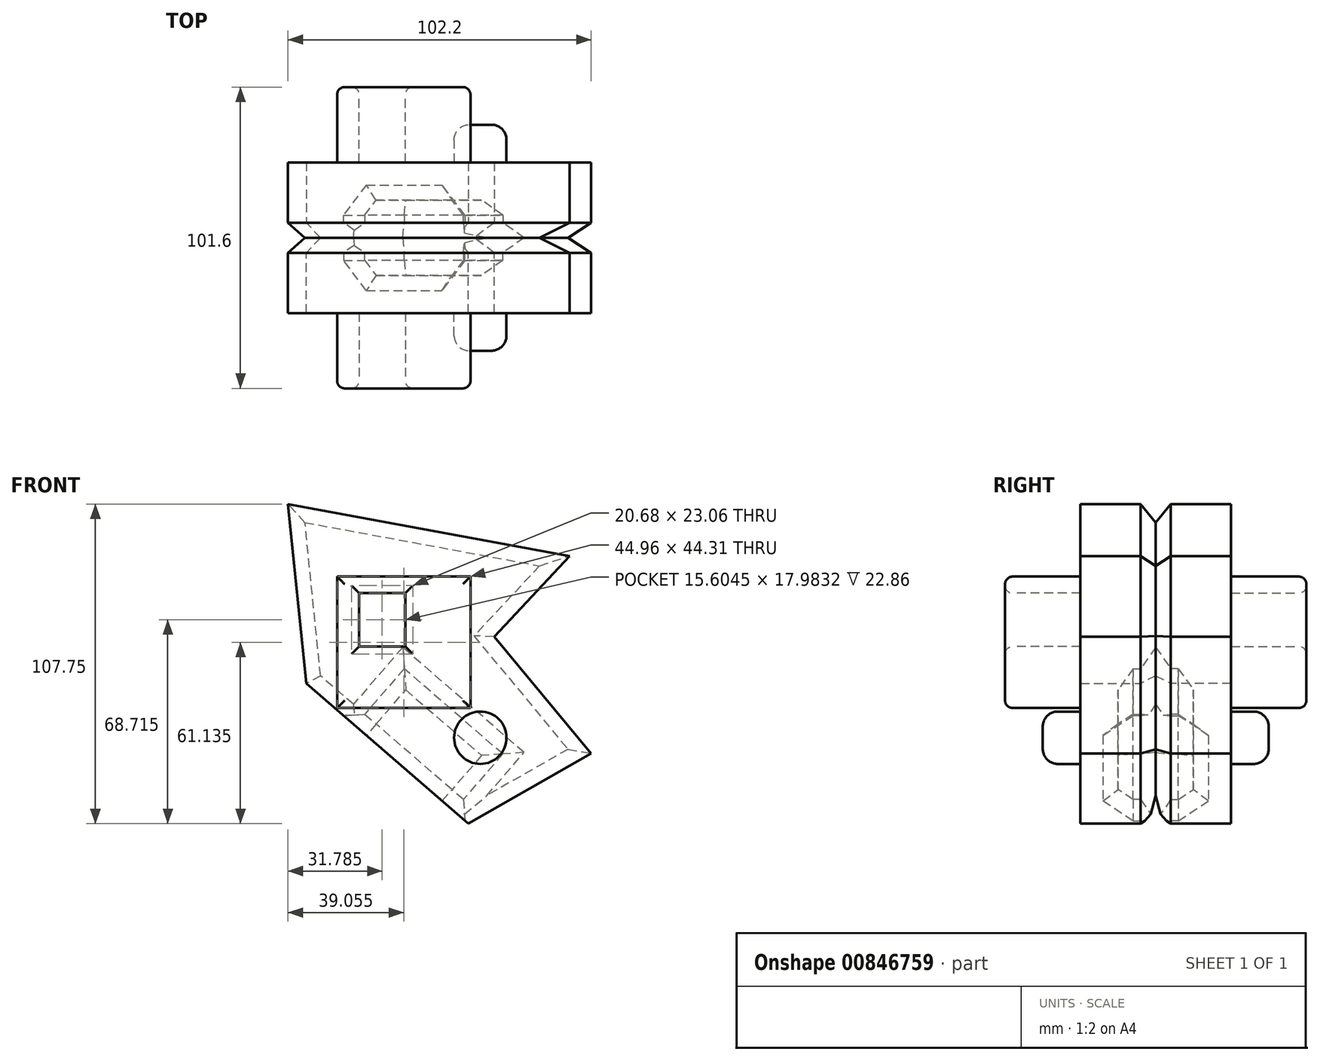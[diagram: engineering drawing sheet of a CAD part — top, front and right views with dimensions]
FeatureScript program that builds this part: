
annotation { "Feature Type Name" : "Feature", "Feature Type Description" : "" }
export const myFeature = defineFeature(function(context is Context, id is Id, definition is map)
    precondition{}
    {
        {
            var Q0;
            Q0=qCreatedBy(makeId("Front.planeOp"),FACE);
            var sketch = newSketch(context, id + "F0", { "sketchPlane" : qUnion([Q0])});
            skLineSegment(sketch, "E0", {"start": v(-47.16, 68.77) * mm, "end": v(47.74, 51.25) * mm});
            skLineSegment(sketch, "E1", {"start": v(47.74, 51.25) * mm, "end": v(22.34, 24.1) * mm});
            skLineSegment(sketch, "E2", {"start": v(22.34, 24.1) * mm, "end": v(55.04, -15.33) * mm});
            skLineSegment(sketch, "E3", {"start": v(55.04, -15.33) * mm, "end": v(13.58, -38.98) * mm});
            skLineSegment(sketch, "E4", {"start": v(13.58, -38.98) * mm, "end": v(-41.03, 8.32) * mm});
            skLineSegment(sketch, "E5", {"start": v(-41.03, 8.32) * mm, "end": v(-47.16, 68.77) * mm});
            skSolve(sketch);
        }
        {
            var Q0;
            Q0=makeQuery(id+"F0.imprint","IMPRINT",FACE,{"disambiguationData":[TD([[makeQuery(id+"F0.imprint","IMPRINT",EDGE,{"derivedFrom":sQuery(id+"F0.wireOp",EDGE,"E0")}),-1.0]])]});
            extrude(context, id + "F1", {"entities" : qUnion([Q0]), "depth" : 25.4 * mm, "offsetDistance" : 25.4 * mm});
        }
        {
            var Q0;
            Q0=makeQuery(id+"F1.opExtrude","CAP_FACE",FACE,{"disambiguationData":[OSD([sQuery(id+"F0.wireOp",EDGE,"E0"),sQuery(id+"F0.wireOp",EDGE,"E1"),sQuery(id+"F0.wireOp",EDGE,"E2"),sQuery(id+"F0.wireOp",EDGE,"E3"),sQuery(id+"F0.wireOp",EDGE,"E4"),sQuery(id+"F0.wireOp",EDGE,"E5")])],"isStart":false});
            var sketch = newSketch(context, id + "F2", { "sketchPlane" : qUnion([Q0])});
            skLineSegment(sketch, "E6.bottom", {"start": v(-30.59, 44.3) * mm, "end": v(14.38, 44.3) * mm});
            skLineSegment(sketch, "E6.top", {"start": v(-30.59, 0) * mm, "end": v(14.38, 0) * mm});
            skLineSegment(sketch, "E6.left", {"start": v(-30.59, 44.3) * mm, "end": v(-30.59, 0) * mm});
            skLineSegment(sketch, "E6.right", {"start": v(14.38, 44.3) * mm, "end": v(14.38, 0) * mm});
            skSolve(sketch);
        }
        {
            var Q0;
            Q0=makeQuery(id+"F2.imprint","IMPRINT",FACE,{"disambiguationData":[TD([[makeQuery(id+"F2.imprint","IMPRINT",EDGE,{"derivedFrom":sQuery(id+"F2.wireOp",EDGE,"E6.bottom")}),-1.0]])]});
            extrude(context, id + "F3", {"entities" : qUnion([Q0]), "operationType" : NewBodyOperationType.ADD, "depth" : 25.4 * mm, "offsetDistance" : 25.4 * mm});
        }
        {
            var Q0;
            Q0=makeQuery(id+"F3.opExtrude","CAP_FACE",FACE,{"disambiguationData":[OSD([sQuery(id+"F2.wireOp",EDGE,"E6.bottom"),sQuery(id+"F2.wireOp",EDGE,"E6.top"),sQuery(id+"F2.wireOp",EDGE,"E6.left"),sQuery(id+"F2.wireOp",EDGE,"E6.right")])],"isStart":false});
            var sketch = newSketch(context, id + "F4", { "sketchPlane" : qUnion([Q0])});
            skLineSegment(sketch, "E7.bottom", {"start": v(-7.57, 20.74) * mm, "end": v(-23.18, 20.74) * mm});
            skLineSegment(sketch, "E7.top", {"start": v(-7.57, 38.73) * mm, "end": v(-23.18, 38.73) * mm});
            skLineSegment(sketch, "E7.left", {"start": v(-7.57, 20.74) * mm, "end": v(-7.57, 38.73) * mm});
            skLineSegment(sketch, "E7.right", {"start": v(-23.18, 20.74) * mm, "end": v(-23.18, 38.73) * mm});
            skPoint(sketch, "E7.middle", {"position": v(-15.37, 29.73) * mm});
            skSolve(sketch);
        }
        {
            var Q0;
            Q0 = qSketchRegion(id + "F4", true);
            extrude(context, id + "F5", {"entities" : qUnion([Q0]), "operationType" : NewBodyOperationType.REMOVE, "oppositeDirection" : true, "depth" : 25.4 * mm, "offsetDistance" : 25.4 * mm});
        }
        {
            var Q0;
            Q0=makeQuery(id+"F1.opExtrude","SWEPT_FACE",FACE,{"disambiguationData":[OSD([sQuery(id+"F0.wireOp",EDGE,"E4")])]});
            var sketch = newSketch(context, id + "F6", { "sketchPlane" : qUnion([Q0])});
            skPoint(sketch, "E8.firstSnap0", {"position": v(-36.46, 12.7) * mm});
            skLineSegment(sketch, "E8.bottom", {"start": v(-14.7, 12.7) * mm, "end": v(29.26, 12.7) * mm});
            skLineSegment(sketch, "E8.top", {"start": v(-14.7, 0) * mm, "end": v(29.26, 0) * mm});
            skLineSegment(sketch, "E8.left", {"start": v(-14.7, 12.7) * mm, "end": v(-14.7, 0) * mm});
            skLineSegment(sketch, "E8.right", {"start": v(29.26, 12.7) * mm, "end": v(29.26, 0) * mm});
            skSolve(sketch);
        }
        {
            var Q0;
            Q0 = qSketchRegion(id + "F6", true);
            extrude(context, id + "F7", {"entities" : qUnion([Q0]), "operationType" : NewBodyOperationType.REMOVE, "oppositeDirection" : true, "depth" : 25.4 * mm, "offsetDistance" : 25.4 * mm});
        }
        {
            var Q0;
            Q0=makeQuery(id+"F1.opExtrude","CAP_FACE",FACE,{"disambiguationData":[OSD([sQuery(id+"F0.wireOp",EDGE,"E0"),sQuery(id+"F0.wireOp",EDGE,"E1"),sQuery(id+"F0.wireOp",EDGE,"E2"),sQuery(id+"F0.wireOp",EDGE,"E3"),sQuery(id+"F0.wireOp",EDGE,"E4"),sQuery(id+"F0.wireOp",EDGE,"E5")])],"isStart":false});
            var sketch = newSketch(context, id + "F8", { "sketchPlane" : qUnion([Q0])});
            skLineSegment(sketch, "E9.bottom", {"start": v(46.14, -13.59) * mm, "end": v(-19.09, -13.59) * mm});
            skLineSegment(sketch, "E9.top", {"start": v(46.14, 0) * mm, "end": v(-19.09, 0) * mm});
            skLineSegment(sketch, "E9.left", {"start": v(46.14, -13.59) * mm, "end": v(46.14, 0) * mm});
            skLineSegment(sketch, "E9.right", {"start": v(-19.09, -13.59) * mm, "end": v(-19.09, 0) * mm});
            skSolve(sketch);
        }
        {
            var Q0;
            Q0=makeQuery(id+"F3.opExtrude","CAP_FACE",FACE,{"disambiguationData":[OSD([sQuery(id+"F2.wireOp",EDGE,"E6.bottom"),sQuery(id+"F2.wireOp",EDGE,"E6.top"),sQuery(id+"F2.wireOp",EDGE,"E6.left"),sQuery(id+"F2.wireOp",EDGE,"E6.right")])],"isStart":false});
            fillet(context, id + "F9", {"entities" : qUnion([Q0]), "radius" : 2.54 * mm, "tangentPropagation" : true, "allowEdgeOverflow" : false});
        }
        {
            var Q0;
            Q0=makeQuery(id+"F1.opExtrude","CAP_FACE",FACE,{"disambiguationData":[OSD([sQuery(id+"F0.wireOp",EDGE,"E0"),sQuery(id+"F0.wireOp",EDGE,"E1"),sQuery(id+"F0.wireOp",EDGE,"E2"),sQuery(id+"F0.wireOp",EDGE,"E3"),sQuery(id+"F0.wireOp",EDGE,"E4"),sQuery(id+"F0.wireOp",EDGE,"E5")])],"isStart":true});
            chamfer(context, id + "F10", {"entities" : qUnion([Q0]), "width" : 5.08 * mm, "tangentPropagation" : true});
        }
        {
            var Q0;
            Q0=makeQuery(id+"F7.boolean.opBoolean","COPY",FACE,{"derivedFrom":makeQuery(id+"F7.opExtrude","SWEPT_FACE",FACE,{"disambiguationData":[OSD([sQuery(id+"F6.wireOp",EDGE,"E8.bottom")])]})});
            chamfer(context, id + "F11", {"entities" : qUnion([Q0]), "width" : 5.08 * mm, "tangentPropagation" : true});
        }
        {
            var Q0;
            {var subQ0=makeQuery(id+"F1.opExtrude","CAP_EDGE",EDGE,{"disambiguationData":[OSD([sQuery(id+"F0.wireOp",EDGE,"E3")])],"isStart":false});Q0=makeQuery(id+"F8.imprint","IMPRINT",FACE,{"disambiguationData":[TD([[makeQuery(id+"F8.imprint","IMPRINT",EDGE,{"derivedFrom":subQ0}),-1.0]])]});}
            var sketch = newSketch(context, id + "F12", { "sketchPlane" : qUnion([Q0])});
            skCircle(sketch, "E10", {"center": v(17.69, -10.03) * mm, "radius": 8.83 * mm});
            skSolve(sketch);
        }
        {
            var Q0;
            Q0 = qSketchRegion(id + "F12", true);
            extrude(context, id + "F13", {"entities" : qUnion([Q0]), "operationType" : NewBodyOperationType.ADD, "depth" : 12.7 * mm, "offsetDistance" : 25.4 * mm});
        }
        {
            var Q0;
            Q0=makeQuery(id+"F13.opExtrude","CAP_EDGE",EDGE,{"disambiguationData":[OSD([sQuery(id+"F12.wireOp",EDGE,"E10")])],"isStart":false});
            fillet(context, id + "F14", {"entities" : qUnion([Q0]), "radius" : 5.08 * mm, "tangentPropagation" : true, "allowEdgeOverflow" : false});
        }
        {
            var Q0;
            Q0=makeQuery(id+"F1.opExtrude","SWEPT_BODY",BODY,{"disambiguationData":[OSD([sQuery(id+"F0.wireOp",EDGE,"E0"),sQuery(id+"F0.wireOp",EDGE,"E1"),sQuery(id+"F0.wireOp",EDGE,"E2"),sQuery(id+"F0.wireOp",EDGE,"E3"),sQuery(id+"F0.wireOp",EDGE,"E4"),sQuery(id+"F0.wireOp",EDGE,"E5")])]});
            var Q1;
            Q1=makeQuery(id+"F1.opExtrude","CAP_FACE",FACE,{"disambiguationData":[OSD([sQuery(id+"F0.wireOp",EDGE,"E0"),sQuery(id+"F0.wireOp",EDGE,"E1"),sQuery(id+"F0.wireOp",EDGE,"E2"),sQuery(id+"F0.wireOp",EDGE,"E3"),sQuery(id+"F0.wireOp",EDGE,"E4"),sQuery(id+"F0.wireOp",EDGE,"E5")])],"isStart":true});
            mirror(context, id + "F15", {"operationType" : NewBodyOperationType.ADD, "entities" : qUnion([Q0]), "mirrorPlane" : qUnion([Q1])});
        }
    });
